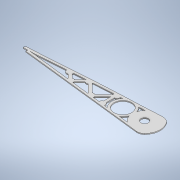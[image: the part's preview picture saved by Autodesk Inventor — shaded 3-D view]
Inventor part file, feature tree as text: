
AUTODESK INVENTOR PART (.ipt)
format: ipt  version: 2022 (Build 260153000, 153)  size: 359,936 bytes
history: native  units: mm
features: extrude x1, sketch x1
ambient origin geometry x8: Origin, YZ Plane, XZ Plane, XY Plane, X Axis, Y Axis, Z Axis, Center Point
bodies: Body1 (feature_tree)
feature tree (2):
  extrude  "Extrusion5"  Depth=1.0mm
  sketch  "Sketch1"  dims[d31=34.456mm d50=368.759386mm d57=16.0mm d69=8.0mm d70=23.0mm d71=8.0mm d73=16.0mm d80=19.0mm d81=16.0mm d82=1.0mm d83=1.0mm d84=1.0mm d85=1.0mm d86=1.0mm d87=0.8mm d88=1.0mm d90=19.0mm d94=5.0mm d95=5.0mm d105=5.0mm d106=5.0mm d108=2.0mm d109=19.0mm d114=5.0mm d115=5.0mm d116=24.0mm d117=2.5mm d118=2.5mm d123=2.5mm d124=2.5mm d125=10.0mm d126=24.0mm d127=24.0mm d128=27.0mm d135=0.5mm d136=45.0deg d139=7.0mm d165=45.0deg d169=27.0mm d175=90.0deg d181=45.0deg d185=7.0mm d186=45.0deg d190=7.0mm d191=45.0deg d197=90.0deg d203=90.0deg d206=7.0mm d207=1.0mm d208=0.0mm]
